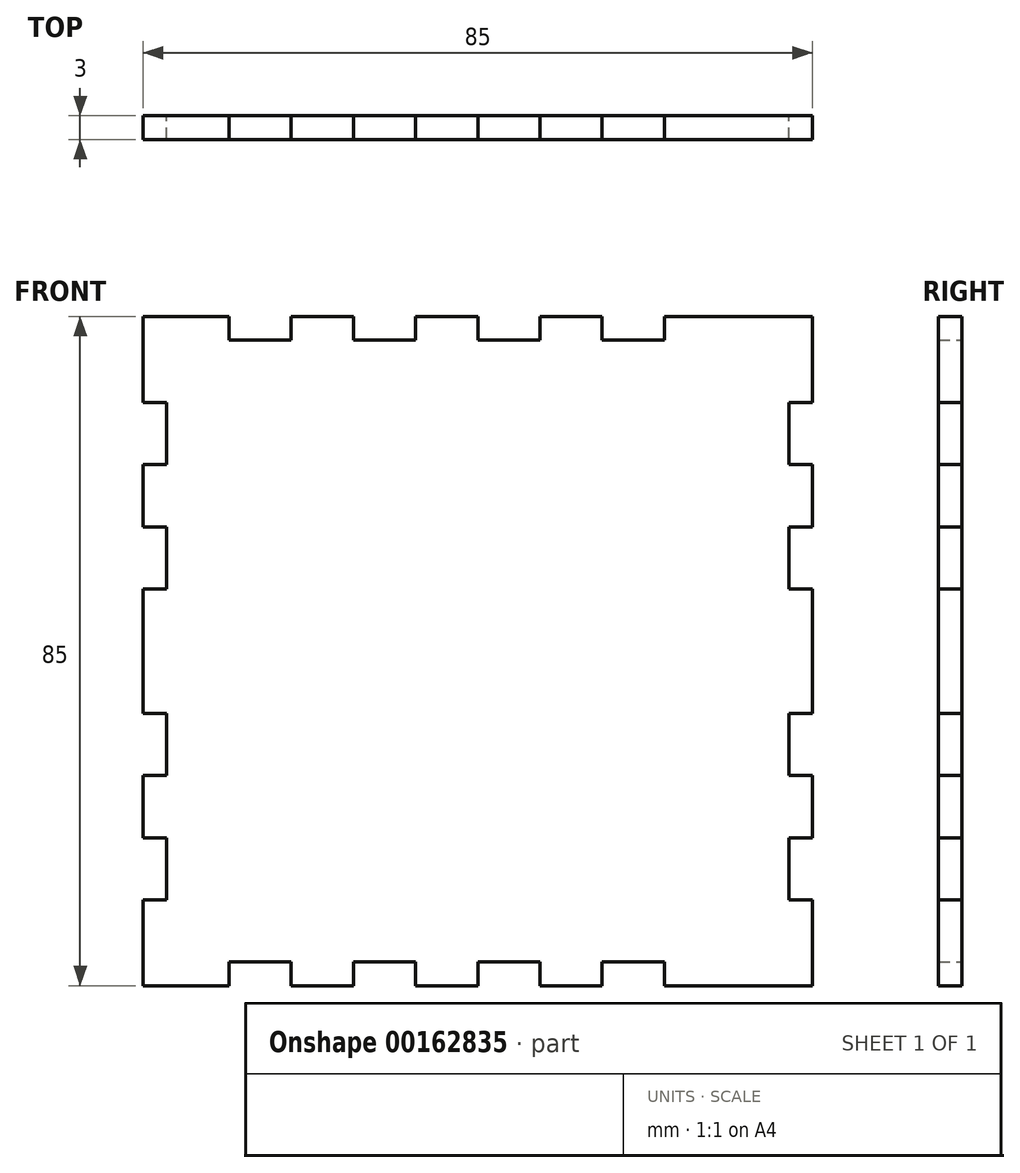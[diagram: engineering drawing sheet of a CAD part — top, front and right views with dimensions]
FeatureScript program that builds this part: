
annotation { "Feature Type Name" : "Feature", "Feature Type Description" : "" }
export const myFeature = defineFeature(function(context is Context, id is Id, definition is map)
    precondition{}
    {
        {
            var Q0;
            Q0=qCreatedBy(makeId("Front.planeOp"),FACE);
            var sketch = newSketch(context, id + "F0", { "sketchPlane" : qUnion([Q0])});
            skLineSegment(sketch, "E0.top", {"start": v(-42.5, -42.5) * mm, "end": v(-31.6, -42.5) * mm});
            skLineSegment(sketch, "E1", {"start": v(-42.5, 0) * mm, "end": v(-39.5, 0) * mm});
            skLineSegment(sketch, "E2", {"start": v(-39.5, -7.9) * mm, "end": v(-42.5, -7.9) * mm});
            skLineSegment(sketch, "E3", {"start": v(-42.5, -15.8) * mm, "end": v(-39.5, -15.8) * mm});
            skLineSegment(sketch, "E4", {"start": v(-42.5, -23.7) * mm, "end": v(-39.5, -23.7) * mm});
            skLineSegment(sketch, "E5", {"start": v(-42.5, -31.6) * mm, "end": v(-39.5, -31.6) * mm});
            skLineSegment(sketch, "E6.trimOffspring", {"start": v(-42.5, 0) * mm, "end": v(-42.5, -7.9) * mm});
            skLineSegment(sketch, "E7.trimOffspring", {"start": v(-42.5, -15.8) * mm, "end": v(-42.5, -23.7) * mm});
            skLineSegment(sketch, "E8.trimOffspring", {"start": v(-42.5, -31.6) * mm, "end": v(-42.5, -42.5) * mm});
            skPoint(sketch, "E0.right.start.orphan", {"position": v(42.5, 42.5) * mm});
            skPoint(sketch, "E9.orphan", {"position": v(42.5, -42.5) * mm});
            skLineSegment(sketch, "E10.MirrorCS", {"start": v(42.5, -31.6) * mm, "end": v(39.5, -31.6) * mm});
            skLineSegment(sketch, "E11.MirrorCS", {"start": v(39.5, -7.9) * mm, "end": v(42.5, -7.9) * mm});
            skLineSegment(sketch, "E12.MirrorCS", {"start": v(42.5, 0) * mm, "end": v(39.5, 0) * mm});
            skLineSegment(sketch, "E13.MirrorCS", {"start": v(42.5, -15.8) * mm, "end": v(39.5, -15.8) * mm});
            skLineSegment(sketch, "E14.MirrorCS", {"start": v(42.5, -23.7) * mm, "end": v(39.5, -23.7) * mm});
            skLineSegment(sketch, "E15.MirrorCS", {"start": v(42.5, -31.6) * mm, "end": v(42.5, -42.5) * mm});
            skLineSegment(sketch, "E16.MirrorCS", {"start": v(42.5, -15.8) * mm, "end": v(42.5, -23.7) * mm});
            skLineSegment(sketch, "E17.MirrorCS", {"start": v(42.5, 0) * mm, "end": v(42.5, -7.9) * mm});
            skLineSegment(sketch, "E18.MirrorCS", {"start": v(42.5, -42.5) * mm, "end": v(23.7, -42.5) * mm});
            skLineSegment(sketch, "E19.trimOffspring", {"start": v(-39.5, -7.9) * mm, "end": v(-39.5, -15.8) * mm});
            skLineSegment(sketch, "E20.trimOffspring", {"start": v(-39.5, -23.7) * mm, "end": v(-39.5, -31.6) * mm});
            skLineSegment(sketch, "E21.trimOffspring", {"start": v(39.5, -23.7) * mm, "end": v(39.5, -31.6) * mm});
            skLineSegment(sketch, "E22.trimOffspring", {"start": v(39.5, -7.9) * mm, "end": v(39.5, -15.8) * mm});
            skLineSegment(sketch, "E23", {"start": v(-31.6, -39.5) * mm, "end": v(-31.6, -42.5) * mm});
            skLineSegment(sketch, "E24", {"start": v(-23.7, -39.5) * mm, "end": v(-23.7, -42.5) * mm});
            skLineSegment(sketch, "E25", {"start": v(-15.8, -39.5) * mm, "end": v(-15.8, -42.5) * mm});
            skLineSegment(sketch, "E26", {"start": v(-7.9, -39.5) * mm, "end": v(-7.9, -42.5) * mm});
            skLineSegment(sketch, "E27", {"start": v(0, -39.5) * mm, "end": v(0, -42.5) * mm});
            skLineSegment(sketch, "E28", {"start": v(7.9, -39.5) * mm, "end": v(7.9, -42.5) * mm});
            skLineSegment(sketch, "E29", {"start": v(15.8, -39.5) * mm, "end": v(15.8, -42.5) * mm});
            skLineSegment(sketch, "E30", {"start": v(23.7, -39.5) * mm, "end": v(23.7, -42.5) * mm});
            skLineSegment(sketch, "E31.trimOffspring", {"start": v(-23.7, -42.5) * mm, "end": v(-15.8, -42.5) * mm});
            skLineSegment(sketch, "E32.trimOffspring", {"start": v(-7.9, -42.5) * mm, "end": v(0, -42.5) * mm});
            skPoint(sketch, "E33.orphan", {"position": v(0, -42.5) * mm});
            skLineSegment(sketch, "E34.trimOffspring", {"start": v(15.8, -42.5) * mm, "end": v(7.9, -42.5) * mm});
            skPoint(sketch, "E35.end.orphan", {"position": v(31.6, -42.5) * mm});
            skPoint(sketch, "E35.start.orphan", {"position": v(31.6, -39.5) * mm});
            skLineSegment(sketch, "E36.trimOffspring", {"start": v(23.7, -39.5) * mm, "end": v(15.8, -39.5) * mm});
            skPoint(sketch, "E37.orphan", {"position": v(39.5, -39.5) * mm});
            skPoint(sketch, "E38.orphan", {"position": v(-39.5, -39.5) * mm});
            skPoint(sketch, "E39.MirrorCS.end.orphan", {"position": v(39.5, 7.9) * mm});
            skPoint(sketch, "E40.MirrorCS.end.orphan", {"position": v(42.5, 7.9) * mm});
            skPoint(sketch, "E41.MirrorCS.start.orphan", {"position": v(42.5, 15.8) * mm});
            skPoint(sketch, "E42.trimOffspring.end.orphan", {"position": v(39.5, 15.8) * mm});
            skPoint(sketch, "E43.MirrorCS.end.orphan", {"position": v(39.5, 23.7) * mm});
            skPoint(sketch, "E44.MirrorCS.end.orphan", {"position": v(42.5, 23.7) * mm});
            skPoint(sketch, "E45.MirrorCS.end.orphan", {"position": v(42.5, 31.6) * mm});
            skPoint(sketch, "E45.MirrorCS.start.orphan", {"position": v(39.5, 31.6) * mm});
            skPoint(sketch, "E46.MirrorCS.end.orphan", {"position": v(0, 39.5) * mm});
            skPoint(sketch, "E47.MirrorCS.end.orphan", {"position": v(0, 42.5) * mm});
            skPoint(sketch, "E48.MirrorCS.end.orphan", {"position": v(42.5, 39.5) * mm});
            skPoint(sketch, "E48.MirrorCS.start.orphan", {"position": v(39.5, 39.5) * mm});
            skPoint(sketch, "E0.left.start.orphan", {"position": v(-42.5, 42.5) * mm});
            skPoint(sketch, "E49.end.orphan", {"position": v(-42.5, 39.5) * mm});
            skPoint(sketch, "E50.left.start.orphan", {"position": v(-39.5, 39.5) * mm});
            skPoint(sketch, "E51.start.orphan", {"position": v(-39.5, 31.6) * mm});
            skPoint(sketch, "E52.trimOffspring.start.orphan", {"position": v(-42.5, 31.6) * mm});
            skPoint(sketch, "E53.start.orphan", {"position": v(-42.5, 23.7) * mm});
            skPoint(sketch, "E54.trimOffspring.start.orphan", {"position": v(-39.5, 23.7) * mm});
            skPoint(sketch, "E55.end.orphan", {"position": v(-39.5, 15.8) * mm});
            skPoint(sketch, "E56.trimOffspring.start.orphan", {"position": v(-42.5, 15.8) * mm});
            skPoint(sketch, "E57.start.orphan", {"position": v(-42.5, 7.9) * mm});
            skPoint(sketch, "E58.trimOffspring.start.orphan", {"position": v(-39.5, 7.9) * mm});
            skLineSegment(sketch, "E59.MirrorCS", {"start": v(0, 39.5) * mm, "end": v(0, 42.5) * mm});
            skLineSegment(sketch, "E60.MirrorCS", {"start": v(23.7, 39.5) * mm, "end": v(23.7, 42.5) * mm});
            skLineSegment(sketch, "E61.MirrorCS", {"start": v(-31.6, 39.5) * mm, "end": v(-31.6, 42.5) * mm});
            skLineSegment(sketch, "E62.MirrorCS", {"start": v(15.8, 39.5) * mm, "end": v(15.8, 42.5) * mm});
            skLineSegment(sketch, "E63.MirrorCS", {"start": v(-15.8, 39.5) * mm, "end": v(-15.8, 42.5) * mm});
            skLineSegment(sketch, "E64.MirrorCS", {"start": v(42.5, 23.7) * mm, "end": v(39.5, 23.7) * mm});
            skLineSegment(sketch, "E65.MirrorCS", {"start": v(-23.7, 39.5) * mm, "end": v(-23.7, 42.5) * mm});
            skLineSegment(sketch, "E66.MirrorCS", {"start": v(42.5, 31.6) * mm, "end": v(39.5, 31.6) * mm});
            skLineSegment(sketch, "E67.MirrorCS", {"start": v(39.5, 7.9) * mm, "end": v(42.5, 7.9) * mm});
            skLineSegment(sketch, "E68.MirrorCS", {"start": v(7.9, 39.5) * mm, "end": v(7.9, 42.5) * mm});
            skLineSegment(sketch, "E69.MirrorCS", {"start": v(-7.9, 39.5) * mm, "end": v(-7.9, 42.5) * mm});
            skLineSegment(sketch, "E70.MirrorCS", {"start": v(42.5, 15.8) * mm, "end": v(39.5, 15.8) * mm});
            skLineSegment(sketch, "E71.MirrorCS", {"start": v(-42.5, 31.6) * mm, "end": v(-39.5, 31.6) * mm});
            skLineSegment(sketch, "E72.MirrorCS", {"start": v(-42.5, 23.7) * mm, "end": v(-39.5, 23.7) * mm});
            skLineSegment(sketch, "E73.MirrorCS", {"start": v(-42.5, 15.8) * mm, "end": v(-39.5, 15.8) * mm});
            skLineSegment(sketch, "E74.MirrorCS", {"start": v(-39.5, 7.9) * mm, "end": v(-42.5, 7.9) * mm});
            skLineSegment(sketch, "E75.MirrorCS", {"start": v(42.5, 15.8) * mm, "end": v(42.5, 23.7) * mm});
            skLineSegment(sketch, "E76.MirrorCS", {"start": v(-39.5, 7.9) * mm, "end": v(-39.5, 15.8) * mm});
            skLineSegment(sketch, "E77.MirrorCS", {"start": v(-23.7, 42.5) * mm, "end": v(-15.8, 42.5) * mm});
            skPoint(sketch, "E78.MirrorP", {"position": v(31.6, 39.5) * mm});
            skLineSegment(sketch, "E79.MirrorCS", {"start": v(42.5, 0) * mm, "end": v(42.5, 7.9) * mm});
            skLineSegment(sketch, "E80.MirrorCS", {"start": v(42.5, 31.6) * mm, "end": v(42.5, 42.5) * mm});
            skLineSegment(sketch, "E81.MirrorCS", {"start": v(23.7, 39.5) * mm, "end": v(15.8, 39.5) * mm});
            skLineSegment(sketch, "E82.MirrorCS", {"start": v(15.8, 42.5) * mm, "end": v(7.9, 42.5) * mm});
            skLineSegment(sketch, "E83.MirrorCS", {"start": v(39.5, 23.7) * mm, "end": v(39.5, 31.6) * mm});
            skLineSegment(sketch, "E84.MirrorCS", {"start": v(-39.5, 23.7) * mm, "end": v(-39.5, 31.6) * mm});
            skPoint(sketch, "E85.MirrorP", {"position": v(31.6, 42.5) * mm});
            skLineSegment(sketch, "E86.MirrorCS", {"start": v(-42.5, 42.5) * mm, "end": v(-31.6, 42.5) * mm});
            skLineSegment(sketch, "E87.MirrorCS", {"start": v(39.5, 7.9) * mm, "end": v(39.5, 15.8) * mm});
            skLineSegment(sketch, "E88.MirrorCS", {"start": v(-7.9, 42.5) * mm, "end": v(0, 42.5) * mm});
            skLineSegment(sketch, "E89.MirrorCS", {"start": v(42.5, 42.5) * mm, "end": v(23.7, 42.5) * mm});
            skLineSegment(sketch, "E90.MirrorCS", {"start": v(-31.6, 39.5) * mm, "end": v(-23.7, 39.5) * mm});
            skLineSegment(sketch, "E91.MirrorCS", {"start": v(-42.5, 0) * mm, "end": v(-42.5, 7.9) * mm});
            skLineSegment(sketch, "E92.MirrorCS", {"start": v(-42.5, 31.6) * mm, "end": v(-42.5, 42.5) * mm});
            skLineSegment(sketch, "E93.MirrorCS", {"start": v(-42.5, 15.8) * mm, "end": v(-42.5, 23.7) * mm});
            skLineSegment(sketch, "E94.trimOffspring", {"start": v(-15.8, 39.5) * mm, "end": v(-7.9, 39.5) * mm});
            skLineSegment(sketch, "E95.trimOffspring", {"start": v(7.9, 39.5) * mm, "end": v(0, 39.5) * mm});
            skLineSegment(sketch, "E96.trimOffspring", {"start": v(-15.8, -39.5) * mm, "end": v(-7.9, -39.5) * mm});
            skLineSegment(sketch, "E97.trimOffspring", {"start": v(7.9, -39.5) * mm, "end": v(0, -39.5) * mm});
            skPoint(sketch, "E98.MirrorCS.start.orphan", {"position": v(0, 30) * mm});
            skPoint(sketch, "E99.orphan", {"position": v(0, -39.5) * mm});
            skLineSegment(sketch, "E100", {"start": v(-31.6, -39.5) * mm, "end": v(-23.7, -39.5) * mm});
            skPoint(sketch, "E101.end.orphan", {"position": v(0, -30) * mm});
            skSolve(sketch);
        }
        {
            var Q0;
            Q0=qSketchRegion(id+"F0",true);
            extrude(context, id + "F1", {"entities" : qUnion([Q0]), "depth" : 3 * mm});
        }
    });
